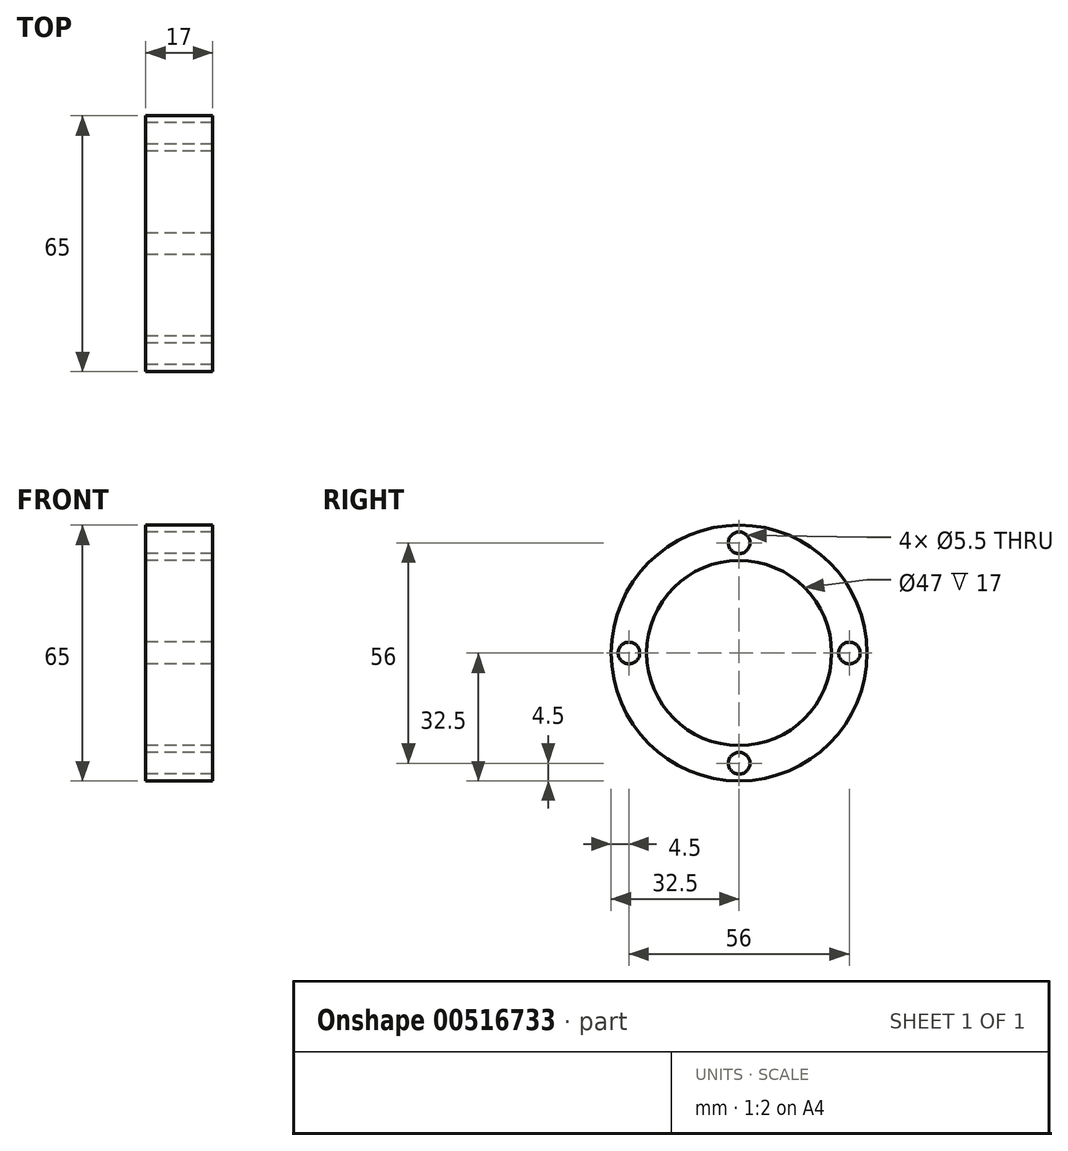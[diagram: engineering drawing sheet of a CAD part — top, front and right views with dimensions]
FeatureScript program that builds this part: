
annotation { "Feature Type Name" : "Feature", "Feature Type Description" : "" }
export const myFeature = defineFeature(function(context is Context, id is Id, definition is map)
    precondition{}
    {
        {
            var Q0;
            Q0=qCreatedBy(makeId("Front.planeOp"),FACE);
            var sketch = newSketch(context, id + "F0", { "sketchPlane" : qUnion([Q0])});
            skLineSegment(sketch, "E0", {"start": v(-34.12, 0) * mm, "end": v(37.4, 0) * mm, "construction": true});
            skLineSegment(sketch, "E1", {"start": v(0, 32.5) * mm, "end": v(0, 23.5) * mm});
            skLineSegment(sketch, "E2", {"start": v(0, 23.5) * mm, "end": v(17, 23.5) * mm});
            skLineSegment(sketch, "E3", {"start": v(17, 23.5) * mm, "end": v(17, 32.5) * mm});
            skLineSegment(sketch, "E4", {"start": v(17, 32.5) * mm, "end": v(0, 32.5) * mm});
            skSolve(sketch);
        }
        {
            var Q0;
            Q0 = qSketchRegion(id + "F0", true);
            var Q1;
            Q1=sQuery(id+"F0.wireOp",EDGE,"E0");
            revolve(context, id + "F1", {"entities" : qUnion([Q0]), "axis" : qUnion([Q1]), "revolveType" : RevolveType.FULL});
        }
        {
            var Q0;
            Q0=makeQuery(id+"F1.opRevolve","SWEPT_FACE",FACE,{"disambiguationData":[OSD([sQuery(id+"F0.wireOp",EDGE,"E1")])]});
            var sketch = newSketch(context, id + "F2", { "sketchPlane" : qUnion([Q0])});
            skCircle(sketch, "E5", {"center": v(0, 0) * mm, "radius": 28 * mm, "construction": true});
            skPoint(sketch, "E6", {"position": v(0, 28) * mm});
            skPoint(sketch, "E7", {"position": v(28, 0) * mm});
            skPoint(sketch, "E8", {"position": v(0, -28) * mm});
            skPoint(sketch, "E9", {"position": v(-28, 0) * mm});
            skSolve(sketch);
        }
        {
            var Q0;
            Q0=sQuery(id+"F2.wireOp",VERTEX,"E6");
            var Q1;
            Q1=sQuery(id+"F2.wireOp",VERTEX,"E7");
            var Q2;
            Q2=sQuery(id+"F2.wireOp",VERTEX,"E8");
            var Q3;
            Q3=sQuery(id+"F2.wireOp",VERTEX,"E9");
            var Q4;
            Q4=makeQuery(id+"F1.opRevolve","SWEPT_BODY",BODY,{"disambiguationData":[OSD([sQuery(id+"F0.wireOp",EDGE,"E1"),sQuery(id+"F0.wireOp",EDGE,"E2"),sQuery(id+"F0.wireOp",EDGE,"NPM4Fhls-3h4F-LKu2-0bDe-jooJPq9ozquu"),sQuery(id+"F0.wireOp",EDGE,"qbmVd184-m6D5-koAs-8WDn-yLaDaJsLGjF8"),sQuery(id+"F0.wireOp",EDGE,"E3"),sQuery(id+"F0.wireOp",EDGE,"E4")])]});
            hole(context, id + "F3", {"style" : HoleStyle.SIMPLE, "endStyle" : HoleEndStyle.THROUGH, "standardTappedOrClearance" : lookupTablePath({ "standard" : "ISO", "fit" : "Normal", "size" : "M5", "type" : "Clearance" }), "standardBlindInLast" : lookupTablePath({ "fit" : "Standard", "standard" : "ISO", "size" : "M5", "type" : "Clearance" }), "holeDiameter" : 5.5 * mm, "isTappedThrough" : true, "tappedDepth" : 12 * mm, "tapClearance" : 3, "locations" : qUnion([Q0, Q1, Q2, Q3]), "scope" : qUnion([Q4])});
        }
    });
